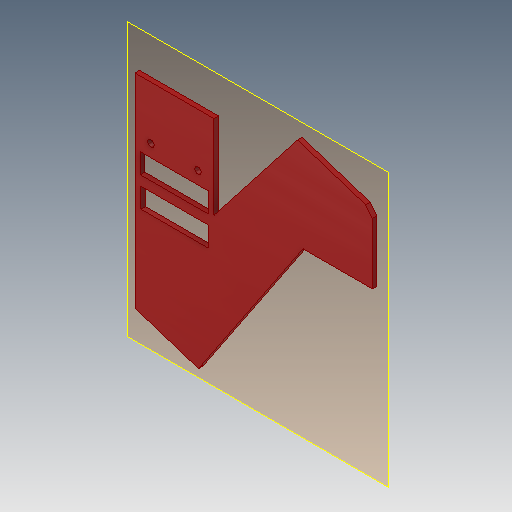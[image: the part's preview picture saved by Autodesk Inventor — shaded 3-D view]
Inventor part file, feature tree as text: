
AUTODESK INVENTOR PART (.ipt)
format: ipt  version: 2019.4 (Build 234330000, 330)  size: 140,288 bytes
history: native  units: mm
features: other x5, extrude x2, sketch x2, reference x2, plane x1
ambient origin geometry x8: Origin, YZ Plane, XZ Plane, XY Plane, X Axis, Y Axis, Z Axis, Center Point
bodies: Solid1 (feature_tree)
feature tree (12):
  plane  "Work Plane1"
  extrude  "Extrusion1"  Depth=2.0mm
  extrude  "Extrusion4"  Depth=10.0mm TaperAngle=0.0deg
  sketch  "Sketch1"  dims[d1=2.0mm d2=0.0mm d13=0.4mm]
  sketch  "Sketch4"  dims[d14=0.4mm d15=10.0mm d16=0.0mm]
  reference  "Referenz3"
  reference  "Referenz4"
  other  "<userpath>\Dropbox\cellSTORM\cellSTORM_v6.iam"
  other  "cellSTORM_v6.iam"
  other  "cellSTORM_v5_microsocpe:1"
  other  "cellSTORM_v5_opticalstage:1"
  other  "cellSTORM_v5.iam"
